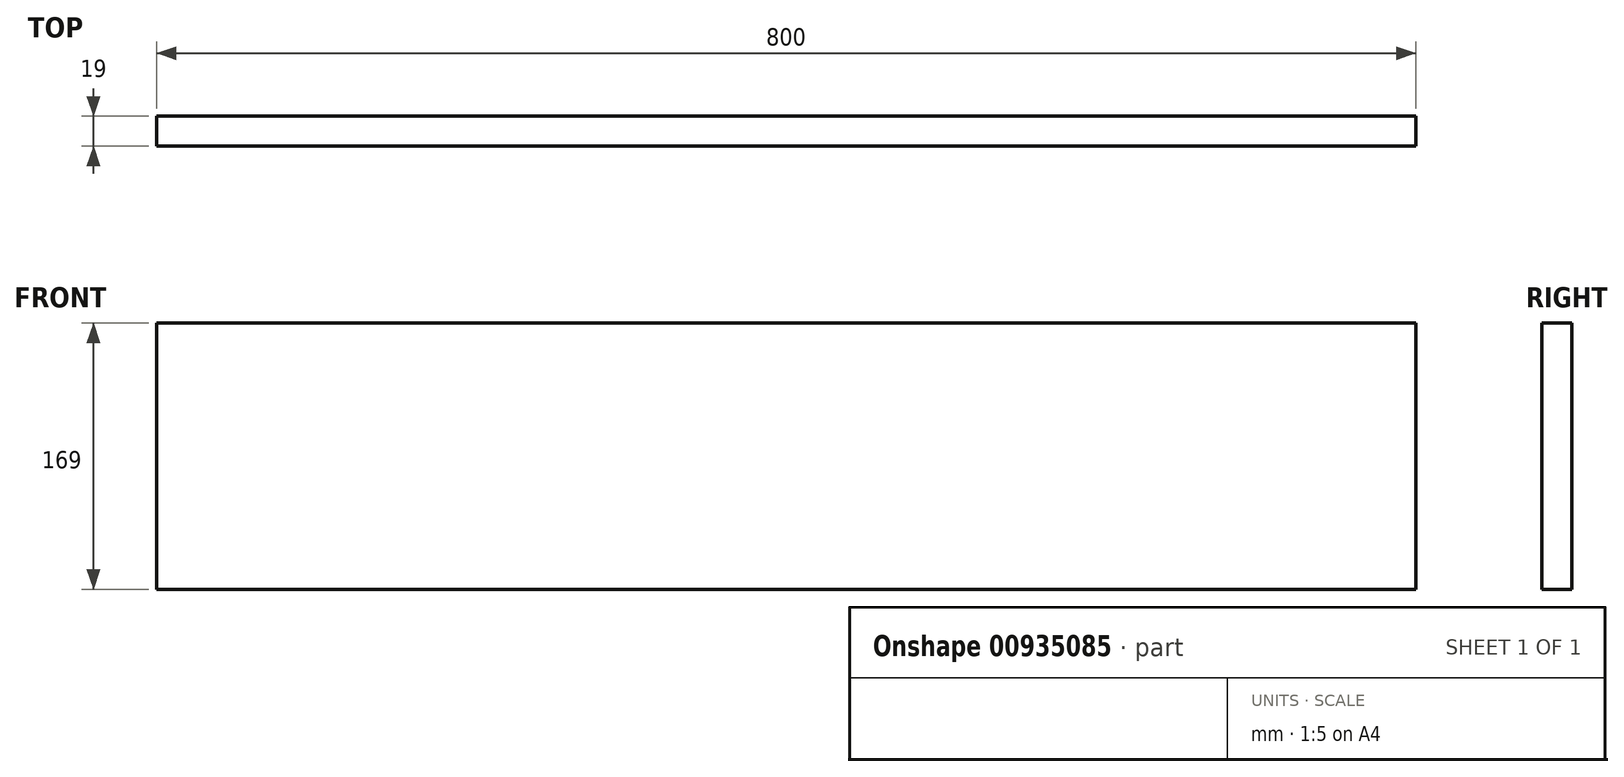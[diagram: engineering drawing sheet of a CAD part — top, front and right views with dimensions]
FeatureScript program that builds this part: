
annotation { "Feature Type Name" : "Feature", "Feature Type Description" : "" }
export const myFeature = defineFeature(function(context is Context, id is Id, definition is map)
    precondition{}
    {
        {
            var Q0;
            Q0=qCreatedBy(makeId("Front.planeOp"),FACE);
            var sketch = newSketch(context, id + "F0", { "sketchPlane" : qUnion([Q0])});
            skLineSegment(sketch, "E0.bottom", {"start": v(0, 0) * mm, "end": v(800, 0) * mm});
            skLineSegment(sketch, "E0.top", {"start": v(0, 169) * mm, "end": v(800, 169) * mm});
            skLineSegment(sketch, "E0.left", {"start": v(0, 0) * mm, "end": v(0, 169) * mm});
            skLineSegment(sketch, "E0.right", {"start": v(800, 0) * mm, "end": v(800, 169) * mm});
            skSolve(sketch);
        }
        {
            var Q0;
            Q0=makeQuery(id+"F0.imprint","IMPRINT",FACE,{"disambiguationData":[TD([[makeQuery(id+"F0.imprint","IMPRINT",EDGE,{"derivedFrom":sQuery(id+"F0.wireOp",EDGE,"E0.bottom")}),1.0]])]});
            extrude(context, id + "F1", {"entities" : qUnion([Q0]), "depth" : 19 * mm, "offsetDistance" : 25 * mm});
        }
    });
